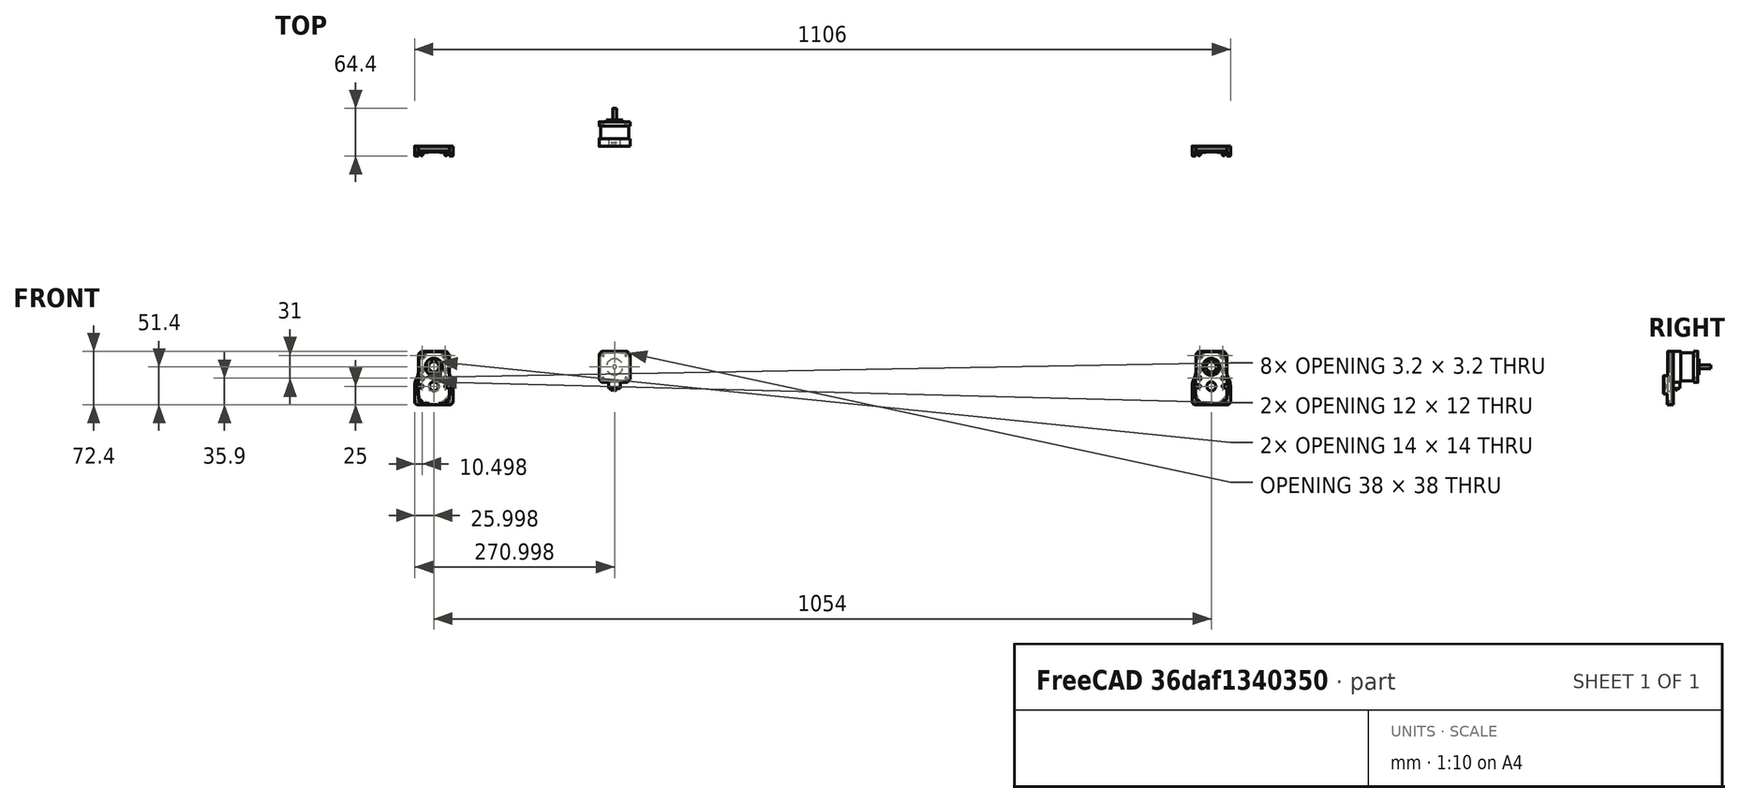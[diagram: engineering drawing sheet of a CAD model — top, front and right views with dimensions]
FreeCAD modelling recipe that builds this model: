
FCSTD DOCUMENT  (FreeCAD 0.18.4R)
Label: servo_adapter
License: All rights reserved
LicenseURL: http://en.wikipedia.org/wiki/All_rights_reserved
objects: Part::Feature×3, Sketcher::SketchObject×3, App::Part×2, PartDesign::Body×1
note: 7 computed .brp shape members not serialized (recipe doc carries the construction recipe); baked Part::Feature solids carry a one-line shape summary decoded from their .brp

FEATURE [Part::Feature] Part__Feature063  label="42步进电机001"
  Placement = pos=(2.84776,-37.0239,62.7501) rot=(0,0,1;0rad)
  shape: bbox 42 x 51.5 x 52.5 mm, 94 faces (baked)
FEATURE [Part::Feature] Part__Feature064  label="减速箱下壳（两侧电机）001"
  Placement = pos=(-242.152,-44.5239,36.35) rot=(0.57735,0.57735,0.57735;4.18879rad)
  shape: bbox 52 x 13.4 x 72.4 mm, 194 faces (baked)
FEATURE [App::Part] _2__1____4_5____________________________________001  label="42+ 1£º4.5减速箱（左右两侧）001"
  Group = -> [Part__Feature063,Part__Feature064]
  Origin = -> Origin004
  Placement = pos=(35.5645,138.951,-86.0279) rot=(-0.57735,0.57735,-0.57735;2.0944rad)
FEATURE [App::Part] Uarm_swift_pro_3D_________  label="Uarm swift pro 3D ÎÄ¼þ"
  Group = -> [_2__1____4_5____________________________________001]
  Origin = -> Origin006
FEATURE [Sketcher::SketchObject] Sketch
  MapMode = 5
  Support = -> [XY_Plane]
  sketch-geometry (87):
    g0: LineSegment StartX=115.605 StartY=360.394 StartZ=0 EndX=119.022 EndY=363.81 EndZ=0
    g1: ArcOfCircle CenterX=118.297 CenterY=364.522 CenterZ=0 NormalX=0 NormalY=0 NormalZ=1 AngleXU=0 Radius=1.01628 StartAngle=5.50629 EndAngle=6.27656
    g2: LineSegment StartX=119.314 StartY=364.515 StartZ=0 EndX=119.314 EndY=397.689 EndZ=0
    g3: ArcOfCircle CenterX=118.297 CenterY=397.682 CenterZ=0 NormalX=0 NormalY=0 NormalZ=1 AngleXU=0 Radius=1.01664 StartAngle=0.007043 EndAngle=0.775031
    g4: LineSegment StartX=119.023 StartY=398.393 StartZ=0 EndX=115.608 EndY=401.809 EndZ=0
    g5: ArcOfCircle CenterX=114.899 CenterY=401.085 CenterZ=0 NormalX=0 NormalY=0 NormalZ=1 AngleXU=0 Radius=1.0134 StartAngle=0.796156 EndAngle=1.56936
    g6: LineSegment StartX=114.901 StartY=402.098 StartZ=0 EndX=91.5364 EndY=402.098 EndZ=0
    g7: ArcOfCircle CenterX=91.8019 CenterY=418.09 CenterZ=0 NormalX=0 NormalY=0 NormalZ=1 AngleXU=0 Radius=15.9934 StartAngle=4.22803 EndAngle=4.69579
    g8: ArcOfCircle CenterX=70.8906 CenterY=377.075 CenterZ=0 NormalX=0 NormalY=0 NormalZ=1 AngleXU=0 Radius=30.0463 StartAngle=1.10614 EndAngle=1.53653
    g9: LineSegment StartX=71.9199 StartY=407.104 StartZ=0 EndX=51.4145 EndY=407.104 EndZ=0
    g10: ArcOfCircle CenterX=51.4486 CenterY=402.57 CenterZ=0 NormalX=0 NormalY=0 NormalZ=1 AngleXU=0 Radius=4.5339 StartAngle=1.57832 EndAngle=3.13447
    g11: LineSegment StartX=46.9148 StartY=402.602 StartZ=0 EndX=46.9148 EndY=359.934 EndZ=0
    g12: LineSegment StartX=55.8064 StartY=402.252 StartZ=0 EndX=86.4224 EndY=402.252 EndZ=0
    g13: LineSegment StartX=61.2125 StartY=402.252 StartZ=0 EndX=61.2125 EndY=407.104 EndZ=0
    g14: LineSegment StartX=71.9149 StartY=406.602 StartZ=0 EndX=61.2125 EndY=406.602 EndZ=0
    g15: ArcOfCircle CenterX=71.2225 CenterY=378.355 CenterZ=0 NormalX=0 NormalY=0 NormalZ=1 AngleXU=0 Radius=28.2549 StartAngle=1.09672 EndAngle=1.54629
    g16: ArcOfCircle CenterX=91.584 CenterY=417.181 CenterZ=0 NormalX=0 NormalY=0 NormalZ=1 AngleXU=0 Radius=15.5892 StartAngle=4.21321 EndAngle=4.71057
    g17: LineSegment StartX=91.5557 StartY=401.592 StartZ=0 EndX=114.901 EndY=401.602 EndZ=0
    g18: ArcOfCircle CenterX=114.902 CenterY=401.11 CenterZ=0 NormalX=0 NormalY=0 NormalZ=1 AngleXU=0 Radius=0.49165 StartAngle=0.776009 EndAngle=1.574
    g19: LineSegment StartX=115.253 StartY=401.455 StartZ=0 EndX=118.668 EndY=398.042 EndZ=0
    g20: ArcOfCircle CenterX=118.284 CenterY=397.677 CenterZ=0 NormalX=0 NormalY=0 NormalZ=1 AngleXU=0 Radius=0.530002 StartAngle=0.019976 EndAngle=0.759868
    g21: LineSegment StartX=118.814 StartY=397.688 StartZ=0 EndX=118.814 EndY=364.518 EndZ=0
    g22: ArcOfCircle CenterX=118.3 CenterY=364.522 CenterZ=0 NormalX=0 NormalY=0 NormalZ=1 AngleXU=0 Radius=0.51421 StartAngle=5.51244 EndAngle=6.27472
    g23: LineSegment StartX=118.669 StartY=364.164 StartZ=0 EndX=115.254 EndY=360.75 EndZ=0
    g24: ArcOfCircle CenterX=114.9 CenterY=361.103 CenterZ=0 NormalX=0 NormalY=0 NormalZ=1 AngleXU=0 Radius=0.499983 StartAngle=4.71318 EndAngle=5.49869
    g25: LineSegment StartX=114.9 StartY=360.603 StartZ=0 EndX=91.5362 EndY=360.603 EndZ=0
    g26: ArcOfCircle CenterX=91.3016 CenterY=345.663 CenterZ=0 NormalX=0 NormalY=0 NormalZ=1 AngleXU=0 Radius=14.939 StartAngle=1.55509 EndAngle=1.90372
    g27: ArcOfCircle CenterX=91.89 CenterY=344.204 CenterZ=0 NormalX=0 NormalY=0 NormalZ=1 AngleXU=0 Radius=16.5104 StartAngle=1.90853 EndAngle=2.06204
    g28: ArcOfCircle CenterX=71.5204 CenterY=382.435 CenterZ=0 NormalX=0 NormalY=0 NormalZ=1 AngleXU=0 Radius=26.8086 StartAngle=4.72698 EndAngle=5.20089
    g29: LineSegment StartX=71.9117 StartY=355.629 StartZ=0 EndX=61.2075 EndY=355.629 EndZ=0
    g30: LineSegment StartX=61.2075 StartY=355.629 StartZ=0 EndX=61.2075 EndY=355.08 EndZ=0
    g31: LineSegment StartX=61.2075 StartY=355.629 StartZ=0 EndX=61.2075 EndY=359.949 EndZ=0
    g32: ArcOfCircle CenterX=51.4235 CenterY=359.601 CenterZ=0 NormalX=0 NormalY=0 NormalZ=1 AngleXU=0 Radius=4.52091 StartAngle=3.06784 EndAngle=4.7078
    g33: LineSegment StartX=51.4027 StartY=355.08 StartZ=0 EndX=61.2075 EndY=355.08 EndZ=0
    g34: LineSegment StartX=61.2075 StartY=355.08 StartZ=0 EndX=71.9321 EndY=355.08 EndZ=0
    g35: ArcOfCircle CenterX=71.3828 CenterY=382.962 CenterZ=0 NormalX=0 NormalY=0 NormalZ=1 AngleXU=0 Radius=27.8874 StartAngle=4.73209 EndAngle=5.19614
    g36: ArcOfCircle CenterX=93.3405 CenterY=341.014 CenterZ=0 NormalX=0 NormalY=0 NormalZ=1 AngleXU=0 Radius=19.4601 StartAngle=1.93429 EndAngle=2.05085
    g37: ArcOfCircle CenterX=91.372 CenterY=346.066 CenterZ=0 NormalX=0 NormalY=0 NormalZ=1 AngleXU=0 Radius=14.0385 StartAngle=1.56037 EndAngle=1.93117
    g38: LineSegment StartX=91.5184 StartY=360.104 StartZ=0 EndX=114.901 EndY=360.104 EndZ=0
    g39: ArcOfCircle CenterX=114.88 CenterY=361.153 CenterZ=0 NormalX=0 NormalY=0 NormalZ=1 AngleXU=0 Radius=1.04915 StartAngle=4.73207 EndAngle=5.47481
    g40: LineSegment StartX=61.2075 StartY=359.949 StartZ=0 EndX=55.8131 EndY=359.953 EndZ=0
    g41: ArcOfCircle CenterX=55.8585 CenterY=362.494 CenterZ=0 NormalX=0 NormalY=0 NormalZ=1 AngleXU=0 Radius=2.54131 StartAngle=3.15954 EndAngle=4.69452
    g42: ArcOfCircle CenterX=51.2954 CenterY=362.933 CenterZ=0 NormalX=0 NormalY=0 NormalZ=1 AngleXU=0 Radius=2.02236 StartAngle=0.0140707 EndAngle=1.56036
    g43: LineSegment StartX=53.3176 StartY=362.448 StartZ=0 EndX=53.3176 EndY=362.961 EndZ=0
    g44: ArcOfCircle CenterX=50.9716 CenterY=367.405 CenterZ=0 NormalX=0 NormalY=0 NormalZ=1 AngleXU=0 Radius=2.45007 StartAngle=3.12818 EndAngle=4.72958
    g45: LineSegment StartX=51.0138 StartY=364.955 StartZ=0 EndX=51.3165 EndY=364.955 EndZ=0
    g46: LineSegment StartX=48.5218 StartY=367.438 StartZ=0 EndX=48.5141 EndY=374.603 EndZ=0
    g47: LineSegment StartX=48.5157 StartY=373.402 StartZ=0 EndX=46.9148 EndY=373.402 EndZ=0
    g48: LineSegment StartX=48.5141 StartY=374.603 StartZ=0 EndX=46.9144 EndY=374.603 EndZ=0
    g49: Circle CenterX=50.9146 CenterY=362.603 CenterZ=0 NormalX=0 NormalY=0 NormalZ=1 AngleXU=0 Radius=0.800456
    g50: Circle CenterX=71.9155 CenterY=364.602 CenterZ=0 NormalX=0 NormalY=0 NormalZ=1 AngleXU=0 Radius=0.785506
    g51: Circle CenterX=71.9162 CenterY=364.598 CenterZ=0 NormalX=0 NormalY=0 NormalZ=1 AngleXU=0 Radius=1.34944
    g52: Circle CenterX=82.8219 CenterY=365.605 CenterZ=0 NormalX=0 NormalY=0 NormalZ=1 AngleXU=0 Radius=1.6124
    g53: Circle CenterX=113.818 CenterY=365.607 CenterZ=0 NormalX=0 NormalY=0 NormalZ=1 AngleXU=0 Radius=1.60824
    g54: Circle CenterX=113.819 CenterY=396.611 CenterZ=0 NormalX=0 NormalY=0 NormalZ=1 AngleXU=0 Radius=1.61161
    g55: Circle CenterX=82.8235 CenterY=396.587 CenterZ=0 NormalX=0 NormalY=0 NormalZ=1 AngleXU=0 Radius=1.61379
    g56: Circle CenterX=71.9195 CenterY=397.605 CenterZ=0 NormalX=0 NormalY=0 NormalZ=1 AngleXU=0 Radius=0.799834
    g57: Circle CenterX=71.9107 CenterY=397.608 CenterZ=0 NormalX=0 NormalY=0 NormalZ=1 AngleXU=0 Radius=1.34556
    g58: Circle CenterX=50.914 CenterY=399.601 CenterZ=0 NormalX=0 NormalY=0 NormalZ=1 AngleXU=0 Radius=0.800455
    g59: Circle CenterX=71.9265 CenterY=381.106 CenterZ=0 NormalX=0 NormalY=0 NormalZ=1 AngleXU=0 Radius=6.01575
    g60: Circle CenterX=98.3337 CenterY=381.091 CenterZ=0 NormalX=0 NormalY=0 NormalZ=1 AngleXU=0 Radius=7.03191
    g61: Circle CenterX=98.3376 CenterY=381.08 CenterZ=0 NormalX=0 NormalY=0 NormalZ=1 AngleXU=0 Radius=11.0251
    g62: Circle CenterX=98.3087 CenterY=381.101 CenterZ=0 NormalX=0 NormalY=0 NormalZ=1 AngleXU=0 Radius=11.5504
    g63: LineSegment StartX=48.519 StartY=387.603 StartZ=0 EndX=46.9148 EndY=387.603 EndZ=0
    g64: LineSegment StartX=48.519 StartY=387.603 StartZ=0 EndX=48.519 EndY=388.803 EndZ=0
    g65: LineSegment StartX=48.519 StartY=388.803 StartZ=0 EndX=46.9148 EndY=388.803 EndZ=0
    g66: LineSegment StartX=48.519 StartY=388.803 StartZ=0 EndX=48.519 EndY=394.752 EndZ=0
    g67: ArcOfCircle CenterX=51.002 CenterY=394.77 CenterZ=0 NormalX=0 NormalY=0 NormalZ=1 AngleXU=0 Radius=2.48313 StartAngle=1.56684 EndAngle=3.14882
    g68: ArcOfCircle CenterX=51.3057 CenterY=399.262 CenterZ=0 NormalX=0 NormalY=0 NormalZ=1 AngleXU=0 Radius=2.00872 StartAngle=4.71747 EndAngle=6.2786
    g69: ArcOfCircle CenterX=55.8101 CenterY=399.756 CenterZ=0 NormalX=0 NormalY=0 NormalZ=1 AngleXU=0 Radius=2.49571 StartAngle=1.57227 EndAngle=3.14309
    g70: LineSegment StartX=51.0119 StartY=397.253 StartZ=0 EndX=51.3159 EndY=397.253 EndZ=0
    g71: LineSegment StartX=53.3144 StartY=399.253 StartZ=0 EndX=53.3144 EndY=399.752 EndZ=0
    g72: LineSegment StartX=50.115 StartY=399.603 StartZ=0 EndX=51.7122 EndY=399.603 EndZ=0
    g73: ArcOfCircle CenterX=67.39 CenterY=399.723 CenterZ=0 NormalX=0 NormalY=0 NormalZ=1 AngleXU=0 Radius=2.52911 StartAngle=0.0133743 EndAngle=1.55281
    g74: LineSegment StartX=69.9189 StartY=399.757 StartZ=0 EndX=69.9189 EndY=397.6 EndZ=0
    g75: ArcOfCircle CenterX=71.9149 CenterY=397.611 CenterZ=0 NormalX=0 NormalY=0 NormalZ=1 AngleXU=0 Radius=1.99611 StartAngle=3.14724 EndAngle=6.27561
    g76: LineSegment StartX=73.911 StartY=397.596 StartZ=0 EndX=73.911 EndY=399.755 EndZ=0
    g77: ArcOfCircle CenterX=76.4189 CenterY=399.744 CenterZ=0 NormalX=0 NormalY=0 NormalZ=1 AngleXU=0 Radius=2.5079 StartAngle=1.57896 EndAngle=3.1373
    g78: LineSegment StartX=71.1198 StartY=397.594 StartZ=0 EndX=72.7193 EndY=397.594 EndZ=0
    g79: LineSegment StartX=61.2075 StartY=359.949 StartZ=0 EndX=86.4194 EndY=359.949 EndZ=0
    g80: LineSegment StartX=86.4194 StartY=359.782 StartZ=0 EndX=86.4194 EndY=359.949 EndZ=0
    g81: ArcOfCircle CenterX=76.4064 CenterY=362.443 CenterZ=0 NormalX=0 NormalY=0 NormalZ=1 AngleXU=0 Radius=2.49397 StartAngle=3.13769 EndAngle=4.70867
    g82: LineSegment StartX=73.9125 StartY=362.452 StartZ=0 EndX=73.9125 EndY=364.609 EndZ=0
    g83: ArcOfCircle CenterX=71.9133 CenterY=364.605 CenterZ=0 NormalX=0 NormalY=0 NormalZ=1 AngleXU=0 Radius=1.99921 StartAngle=0.001968 EndAngle=3.14243
    g84: LineSegment StartX=69.9141 StartY=364.603 StartZ=0 EndX=69.9141 EndY=362.444 EndZ=0
    g85: ArcOfCircle CenterX=67.4108 CenterY=362.452 CenterZ=0 NormalX=0 NormalY=0 NormalZ=1 AngleXU=0 Radius=2.50329 StartAngle=4.71401 EndAngle=6.27982
    g86: LineSegment StartX=71.13 StartY=364.593 StartZ=0 EndX=72.7099 EndY=364.593 EndZ=0
  constraints (111):
    c: Coincident(g1,g0)
    c: Coincident(g2,g1)
    c: Vertical(g2)
    c: Coincident(g3,g2)
    c: Coincident(g4,g3)
    c: Coincident(g5,g4)
    c: Coincident(g6,g5)
    c: Horizontal(g6)
    c: Coincident(g7,g6)
    c: Coincident(g8,g7)
    c: Coincident(g9,g8)
    c: Horizontal(g9)
    c: Coincident(g10,g9)
    c: Coincident(g11,g10)
    c: Vertical(g11)
    c: Horizontal(g12)
    c: PointOnObject(g13,g12)
    c: PointOnObject(g13,g9)
    c: Vertical(g13)
    c: PointOnObject(g14,g13)
    c: Horizontal(g14)
    c: Coincident(g15,g14)
    c: Coincident(g16,g15)
    c: Coincident(g17,g16)
    c: Coincident(g18,g17)
    c: Coincident(g19,g18)
    c: Coincident(g20,g19)
    c: Coincident(g21,g20)
    c: Vertical(g21)
    c: Coincident(g22,g21)
    c: Coincident(g23,g22)
    c: Coincident(g24,g23)
    c: Coincident(g25,g24)
    c: Horizontal(g25)
    c: Coincident(g27,g26)
    c: Coincident(g28,g27)
    c: Coincident(g29,g28)
    c: Horizontal(g29)
    c: Coincident(g30,g29)
    c: Vertical(g30)
    c: Coincident(g31,g29)
    c: Vertical(g31)
    c: Coincident(g32,g11)
    c: Coincident(g33,g32)
    c: Coincident(g33,g30)
    c: Horizontal(g33)
    c: Coincident(g34,g30)
    c: Horizontal(g34)
    c: Coincident(g35,g34)
    c: Coincident(g36,g35)
    c: Coincident(g37,g36)
    c: Coincident(g38,g37)
    c: Horizontal(g38)
    c: Coincident(g39,g38)
    c: Coincident(g39,g0)
    c: Coincident(g40,g31)
    c: Coincident(g41,g40)
    c: Coincident(g43,g41)
    c: Coincident(g43,g42)
    c: Vertical(g43)
    c: Coincident(g45,g42)
    c: Horizontal(g45)
    c: Coincident(g46,g44)
    c: PointOnObject(g47,g11)
    c: Horizontal(g47)
    c: Coincident(g48,g46)
    c: Horizontal(g48)
    c: PointOnObject(g63,g11)
    c: Horizontal(g63)
    c: Coincident(g64,g63)
    c: Vertical(g64)
    c: Coincident(g65,g64)
    c: PointOnObject(g65,g11)
    c: Horizontal(g65)
    c: Coincident(g66,g64)
    c: Vertical(g66)
    c: Coincident(g67,g66)
    c: Coincident(g69,g12)
    c: Coincident(g70,g67)
    c: Coincident(g70,g68)
    c: Horizontal(g70)
    c: Coincident(g71,g68)
    c: Coincident(g71,g69)
    c: Vertical(g71)
    c: Horizontal(g72)
    c: PointOnObject(g73,g12)
    c: Coincident(g74,g73)
    c: Vertical(g74)
    c: Coincident(g75,g74)
    c: Coincident(g76,g75)
    c: Vertical(g76)
    c: Coincident(g77,g76)
    c: PointOnObject(g77,g12)
    c: PointOnObject(g78,g56)
    c: PointOnObject(g78,g56)
    c: Horizontal(g78)
    c: Coincident(g79,g31)
    c: Horizontal(g79)
    c: Coincident(g80,g26)
    c: Coincident(g80,g79)
    c: Vertical(g80)
    c: PointOnObject(g81,g79)
    c: Coincident(g82,g81)
    c: Vertical(g82)
    c: Coincident(g83,g82)
    c: Coincident(g84,g83)
    c: Vertical(g84)
    c: Coincident(g85,g84)
    c: PointOnObject(g85,g79)
    c: PointOnObject(g86,g50)
    c: Horizontal(g86)
FEATURE [Sketcher::SketchObject] Sketch002
  MapMode = 3
  Placement = pos=(-242.152,-44.5239,36.35) rot=(0,-1,0;1.5708rad)
  Support = -> [Part__Feature064]
  sketch-geometry (37):
    g0: LineSegment StartX=-85.8541 StartY=451.627 StartZ=0 EndX=-72.955 EndY=451.627 EndZ=0
    g1: LineSegment StartX=-72.955 StartY=451.627 StartZ=0 EndX=-72.4541 EndY=451.127 EndZ=0
    g2: LineSegment StartX=-72.4541 StartY=451.127 StartZ=0 EndX=-72.4541 EndY=446.777 EndZ=0
    g3: LineSegment StartX=-72.4541 StartY=446.777 StartZ=0 EndX=-77.4439 EndY=446.777 EndZ=0
    g4: LineSegment StartX=-77.4439 StartY=446.777 StartZ=0 EndX=-77.4439 EndY=433.327 EndZ=0
    g5: ArcOfCircle CenterX=-75.8718 CenterY=432.133 CenterZ=0 NormalX=0 NormalY=0 NormalZ=1 AngleXU=0 Radius=1.9745 StartAngle=2.4918 EndAngle=3.1438
    g6: LineSegment StartX=-77.8463 StartY=432.128 StartZ=0 EndX=-77.8463 EndY=419.123 EndZ=0
    g7: ArcOfCircle CenterX=-75.8736 CenterY=419.121 CenterZ=0 NormalX=0 NormalY=0 NormalZ=1 AngleXU=0 Radius=1.97271 StartAngle=3.14099 EndAngle=3.79177
    g8: LineSegment StartX=-77.4438 StartY=417.927 StartZ=0 EndX=-77.4438 EndY=411.112 EndZ=0
    g9: LineSegment StartX=-77.4438 StartY=411.112 StartZ=0 EndX=-74.0543 EndY=411.112 EndZ=0
    g10: LineSegment StartX=-74.0543 StartY=411.112 StartZ=0 EndX=-74.0543 EndY=410.468 EndZ=0
    g11: LineSegment StartX=-74.0543 StartY=410.468 StartZ=0 EndX=-72.854 EndY=410.468 EndZ=0
    g12: LineSegment StartX=-72.854 StartY=410.468 StartZ=0 EndX=-72.854 EndY=407.787 EndZ=0
    g13: LineSegment StartX=-72.854 StartY=407.787 StartZ=0 EndX=-74.0543 EndY=407.787 EndZ=0
    g14: LineSegment StartX=-74.0543 StartY=407.787 StartZ=0 EndX=-74.0543 EndY=404.467 EndZ=0
    g15: LineSegment StartX=-74.0543 StartY=404.467 StartZ=0 EndX=-72.454 EndY=404.467 EndZ=0
    g16: LineSegment StartX=-72.454 StartY=404.467 StartZ=0 EndX=-72.454 EndY=400.127 EndZ=0
    g17: LineSegment StartX=-72.454 StartY=400.127 StartZ=0 EndX=-72.954 EndY=399.627 EndZ=0
    g18: LineSegment StartX=-72.954 StartY=399.627 StartZ=0 EndX=-85.8541 EndY=399.627 EndZ=0
    g19: LineSegment StartX=-85.8541 StartY=399.627 StartZ=0 EndX=-85.8541 EndY=451.627 EndZ=0
    g20: LineSegment StartX=-77.4439 StartY=446.777 StartZ=0 EndX=-77.4439 EndY=451.627 EndZ=0
    g21: LineSegment StartX=-85.8524 StartY=447.115 StartZ=0 EndX=-77.4439 EndY=447.115 EndZ=0
    g22: LineSegment StartX=-74.0539 StartY=446.777 StartZ=0 EndX=-74.0539 EndY=440.142 EndZ=0
    g23: LineSegment StartX=-74.0539 StartY=440.142 StartZ=0 EndX=-77.4439 EndY=440.142 EndZ=0
    g24: LineSegment StartX=-77.4439 StartY=442.127 StartZ=0 EndX=-74.0539 EndY=442.127 EndZ=0
    g25: LineSegment StartX=-74.0539 StartY=442.127 StartZ=0 EndX=-72.8542 EndY=442.127 EndZ=0
    g26: LineSegment StartX=-72.8542 StartY=442.127 StartZ=0 EndX=-72.8542 EndY=443.467 EndZ=0
    g27: LineSegment StartX=-72.8542 StartY=443.467 StartZ=0 EndX=-74.0539 EndY=443.467 EndZ=0
    g28: LineSegment StartX=-72.8542 StartY=442.127 StartZ=0 EndX=-72.8542 EndY=440.787 EndZ=0
    g29: LineSegment StartX=-72.8542 StartY=440.787 StartZ=0 EndX=-74.0539 EndY=440.787 EndZ=0
    g30: LineSegment StartX=-77.4438 StartY=411.112 StartZ=0 EndX=-77.4438 EndY=399.627 EndZ=0
    g31: LineSegment StartX=-74.0543 StartY=404.467 StartZ=0 EndX=-77.4438 EndY=404.467 EndZ=0
    g32: LineSegment StartX=-77.4438 StartY=406.984 StartZ=0 EndX=-74.0543 EndY=406.984 EndZ=0
    g33: LineSegment StartX=-77.4438 StartY=409.128 StartZ=0 EndX=-72.854 EndY=409.128 EndZ=0
    g34: LineSegment StartX=-74.0543 StartY=410.468 StartZ=0 EndX=-74.0543 EndY=409.128 EndZ=0
    g35: LineSegment StartX=-74.0543 StartY=409.128 StartZ=0 EndX=-74.0543 EndY=407.787 EndZ=0
    g36: LineSegment StartX=-77.4438 StartY=404.11 StartZ=0 EndX=-85.8429 EndY=404.11 EndZ=0
  constraints (79):
    c: Horizontal(g0)
    c: Coincident(g1,g0)
    c: Coincident(g2,g1)
    c: Vertical(g2)
    c: Coincident(g3,g2)
    c: Horizontal(g3)
    c: Coincident(g4,g3)
    c: Vertical(g4)
    c: Coincident(g5,g4)
    c: Coincident(g6,g5)
    c: Vertical(g6)
    c: Coincident(g7,g6)
    c: Coincident(g8,g7)
    c: Vertical(g8)
    c: Coincident(g9,g8)
    c: Horizontal(g9)
    c: Coincident(g10,g9)
    c: Vertical(g10)
    c: Coincident(g11,g10)
    c: Horizontal(g11)
    c: Coincident(g12,g11)
    c: Vertical(g12)
    c: Coincident(g13,g12)
    c: Horizontal(g13)
    c: Coincident(g14,g13)
    c: Vertical(g14)
    c: Coincident(g15,g14)
    c: Horizontal(g15)
    c: Coincident(g16,g15)
    c: Vertical(g16)
    c: Coincident(g17,g16)
    c: Coincident(g18,g17)
    c: Horizontal(g18)
    c: Coincident(g19,g18)
    c: Coincident(g19,g0)
    c: Vertical(g19)
    c: Coincident(g20,g3)
    c: PointOnObject(g20,g0)
    c: Vertical(g20)
    c: PointOnObject(g21,g20)
    c: Horizontal(g21)
    c: PointOnObject(g22,g3)
    c: Vertical(g22)
    c: Coincident(g23,g22)
    c: PointOnObject(g23,g4)
    c: Horizontal(g23)
    c: PointOnObject(g24,g4)
    c: PointOnObject(g24,g22)
    c: Horizontal(g24)
    c: Coincident(g25,g24)
    c: Horizontal(g25)
    c: Vertical(g26)
    c: Coincident(g27,g26)
    c: PointOnObject(g27,g22)
    c: Horizontal(g27)
    c: Vertical(g28)
    c: Coincident(g29,g28)
    c: PointOnObject(g29,g22)
    c: Horizontal(g29)
    c: Coincident(g30,g8)
    c: PointOnObject(g30,g18)
    c: Vertical(g30)
    c: Coincident(g31,g14)
    c: PointOnObject(g31,g30)
    c: Horizontal(g31)
    c: PointOnObject(g32,g30)
    c: PointOnObject(g32,g14)
    c: Horizontal(g32)
    c: PointOnObject(g33,g30)
    c: PointOnObject(g33,g12)
    c: Horizontal(g33)
    c: Coincident(g34,g10)
    c: PointOnObject(g34,g33)
    c: Vertical(g34)
    c: Coincident(g35,g34)
    c: Coincident(g35,g13)
    c: Vertical(g35)
    c: PointOnObject(g36,g30)
    c: Horizontal(g36)
FEATURE [PartDesign::Body] Body
  Group = -> [Sketch,Sketch002]
  Origin = -> Origin
FEATURE [Part::Feature] Part__Feature065  label="减速箱下壳（两侧电机）002"
  Placement = pos=(811.848,-44.5239,36.3501) rot=(0.57735,0.57735,0.57735;4.18879rad)
  shape: bbox 52 x 13.4 x 72.4 mm, 194 faces (baked)
FEATURE [Sketcher::SketchObject] Sketch003
  ExternalGeometry = -> [Part__Feature065]
  MapMode = 2
  Placement = pos=(811.848,-44.5239,36.3501) rot=(0.57735,0.57735,0.57735;4.18879rad)
  Support = -> [Part__Feature065]
  sketch-geometry (1):
    g0: LineSegment StartX=-25 StartY=21.5 StartZ=0 EndX=-25 EndY=-21.5063 EndZ=0
  constraints (2):
    c: Coincident(g0,g-3)
    c: Vertical(g0)
